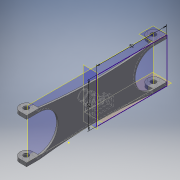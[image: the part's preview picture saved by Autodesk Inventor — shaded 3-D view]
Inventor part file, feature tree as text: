
AUTODESK INVENTOR PART (.ipt)
format: ipt  version: 2017 (Build 210142000, 142)  size: 613,888 bytes
history: native  units: mm
features: sketch x19, extrude x18, move_body x12, projected_geometry x8, direct_edit x6, other x5, plane x4, fillet x4, hole x2, mirror x1, reference x1
ambient origin geometry x8: Origin, YZ Plane, XZ Plane, XY Plane, X Axis, Y Axis, Z Axis, Center Point
bodies: Solid1 (feature_tree)
feature tree (80):
  plane  "Work Plane1"
  extrude  "Extrusion1"  Depth=7.0mm
  fillet  "Fillet1"  Radius=4.0mm
  plane  "Work Plane2"
  extrude  "Extrusion2"  Depth=2.0mm TaperAngle=0.0deg
  plane  "Work Plane3"
  mirror  "Mirror1"
  extrude  "Extrusion3"  Depth=4.0mm
  extrude  "Extrusion4"  Depth=12.0mm
  extrude  "Extrusion5"  Depth=1.0mm
  extrude  "Extrusion6"  Depth=12.0mm
  sketch  "Sketch8"  dims[d22=22.2mm d23=1.0mm]
  direct_edit  "Direct Edit1"
  extrude  "Extrusion7"  Depth=1.0mm
  extrude  "Extrusion8"  Depth=5.0mm
  extrude  "Extrusion9"  Depth=4.0mm
  extrude  "Extrusion10"  Depth=2.0mm
  direct_edit  "Direct Edit2"
  fillet  "Fillet3"  Radius=2.0mm
  hole  "Hole1"  [1 undecoded]
  plane  "Work Plane4"
  extrude  "Extrusion11"  Depth=22.0mm
  extrude  "Extrusion12"  Depth=500.0mm
  direct_edit  "Direct Edit3"
  hole  "Hole2"  [1 undecoded]
  direct_edit  "Direct Edit4"
  direct_edit  "Direct Edit5"
  extrude  "Extrusion13"  Depth=5.0mm TaperAngle=0.0deg
  direct_edit  "Direct Edit6"
  extrude  "Extrusion14"  Depth=2.0mm TaperAngle=0.0deg
  extrude  "Extrusion15"  Depth=2.0mm
  fillet  "Fillet5"  Radius=10.0mm
  fillet  "Fillet6"  Radius=1.0mm
  extrude  "Extrusion16"  Depth=3.0mm TaperAngle=0.0deg
  extrude  "Extrusion17"  TaperAngle=0.0deg  [1 undecoded]
  extrude  "Extrusion18"  TaperAngle=0.0deg  [1 undecoded]
  sketch  "Sketch1"  dims[d2=4.0mm d3=0.0mm d4=7.0mm d5=4.0mm d6=0.0mm]
  reference  "Reference1"
  sketch  "Sketch2"  dims[d9=164.0mm d10=2.0mm d11=0.0mm]
  projected_geometry  "Projected Loop1"
  sketch  "Sketch4"  dims[d12=52.0mm d13=4.0mm]
  sketch  "Sketch5"  dims[d14=10.0mm d15=12.0mm]
  sketch  "Sketch6"  dims[d16=15.0mm d17=1.0mm]
  sketch  "Sketch7"  dims[d18=12.0mm d19=0.0mm d21=8.5mm]
  sketch  "Sketch9"  dims[d24=10.0mm d25=0.0mm d26=5.0mm]
  projected_geometry  "Projected Loop2"
  sketch  "Sketch10"  dims[d27=1.0mm d28=0.0mm d29=4.0mm]
  projected_geometry  "Projected Loop3"
  sketch  "Sketch11"  dims[d30=4.0mm d31=2.0mm d32=2.0mm]
  sketch  "Sketch12"  dims[d33=0.0mm d34=0.0mm d35=1.0mm d36=1.0mm]
  sketch  "Sketch13"  dims[d37=3.5mm d38=0.0mm d39=22.0mm]
  sketch  "Sketch15"  dims[d40=22.0mm d41=500.0mm]
  sketch  "Sketch16"  dims[d42=500.0mm d43=3.5mm d44=0.0mm]
  sketch  "Sketch18"  dims[d45=2.0mm d46=5.0mm d47=0.0mm]
  projected_geometry  "Projected Loop5"
  projected_geometry  "Projected Loop6"
  projected_geometry  "Projected Loop7"
  projected_geometry  "Projected Loop8"
  sketch  "Sketch23"  dims[d48=2.0mm d49=6.0mm d50=0.0mm]
  projected_geometry  "Projected Loop9"
  sketch  "Sketch25"  dims[d51=0.0mm d52=0.0mm d53=3.0mm d54=2.0mm d55=10.0mm d56=10.0mm]
  sketch  "Sketch26"  dims[d57=3.0mm d58=6.0mm d59=4.0mm d60=2.0mm d61=90.0deg d62=0.5mm d63=20.594885mm d64=1.0mm]
  sketch  "Sketch27"  dims[d68=6.0mm d69=0.0mm d70=6.0mm d71=0.0mm d72=0.0mm d73=0.0mm d74=-3.5mm d75=0.0mm d76=0.0mm d77=-0.25mm d78=0.0mm d79=0.0mm d80=-0.25mm d81=0.0mm d82=0.0mm d83=-0.25mm d84=0.0mm d85=0.0mm d86=-0.25mm d87=4.0mm d88=5.0mm d89=6.0mm d90=4.0mm d91=2.0mm d92=90.0deg d93=10.0mm d94=0.0mm d95=0.0mm d96=0.0mm d97=-5.0mm d98=0.0mm d99=0.0mm d100=5.0mm d101=0.0mm d102=0.0mm d103=-5.0mm d104=3.0mm d105=0.0mm d106=0.0mm d107=0.0mm d108=-2.0mm d109=0.0mm d110=0.0mm d111=-2.0mm d112=1.0mm d113=0.0mm d114=1.5mm d115=10.75mm d116=0.0mm d118=0.0mm d119=6.0mm d120=6.0mm d121=0.0mm d122=0.0mm d123=6.0mm d124=0.0mm d125=6.0mm d126=1.0mm d127=45.0mm d128=31.0mm d129=0.0mm d130=0.0mm d131=1.0mm d132=7.0mm d133=0.0mm d136=1.0mm d137=1.0mm d138=3.0mm d139=0.0mm d140=1.0mm d141=1.0mm d142=1.0mm d143=2.0mm d144=1.0mm d145=1.0mm d146=1.0mm d147=1.0mm d148=3.0mm d149=0.0mm]
  parser-record x1  (decoder bookkeeping rows leaked as tree rows — omitted from the tree; the rows remain in map.json)
  other  "assembly_full.iam"
  other  "top_right:1"
  move_body  "Move1"
  move_body  "Move2"
  move_body  "Move3"
  move_body  "Move4"
  move_body  "Move5"
  move_body  "Move6"
  move_body  "Move7"
  move_body  "Move8"
  move_body  "Move9"
  move_body  "Move10"
  move_body  "Move11"
  move_body  "Move12"
  other  "Assembly4"
  other  "cap:1"
note: 4 required parameter values undecoded (feature->parameter linkage not recoverable at this tier; creation-order binding heuristic only, values carry confidence <= 0.55)
note: 1 file-system path scrubbed to <path> (originals preserved in map.json)
